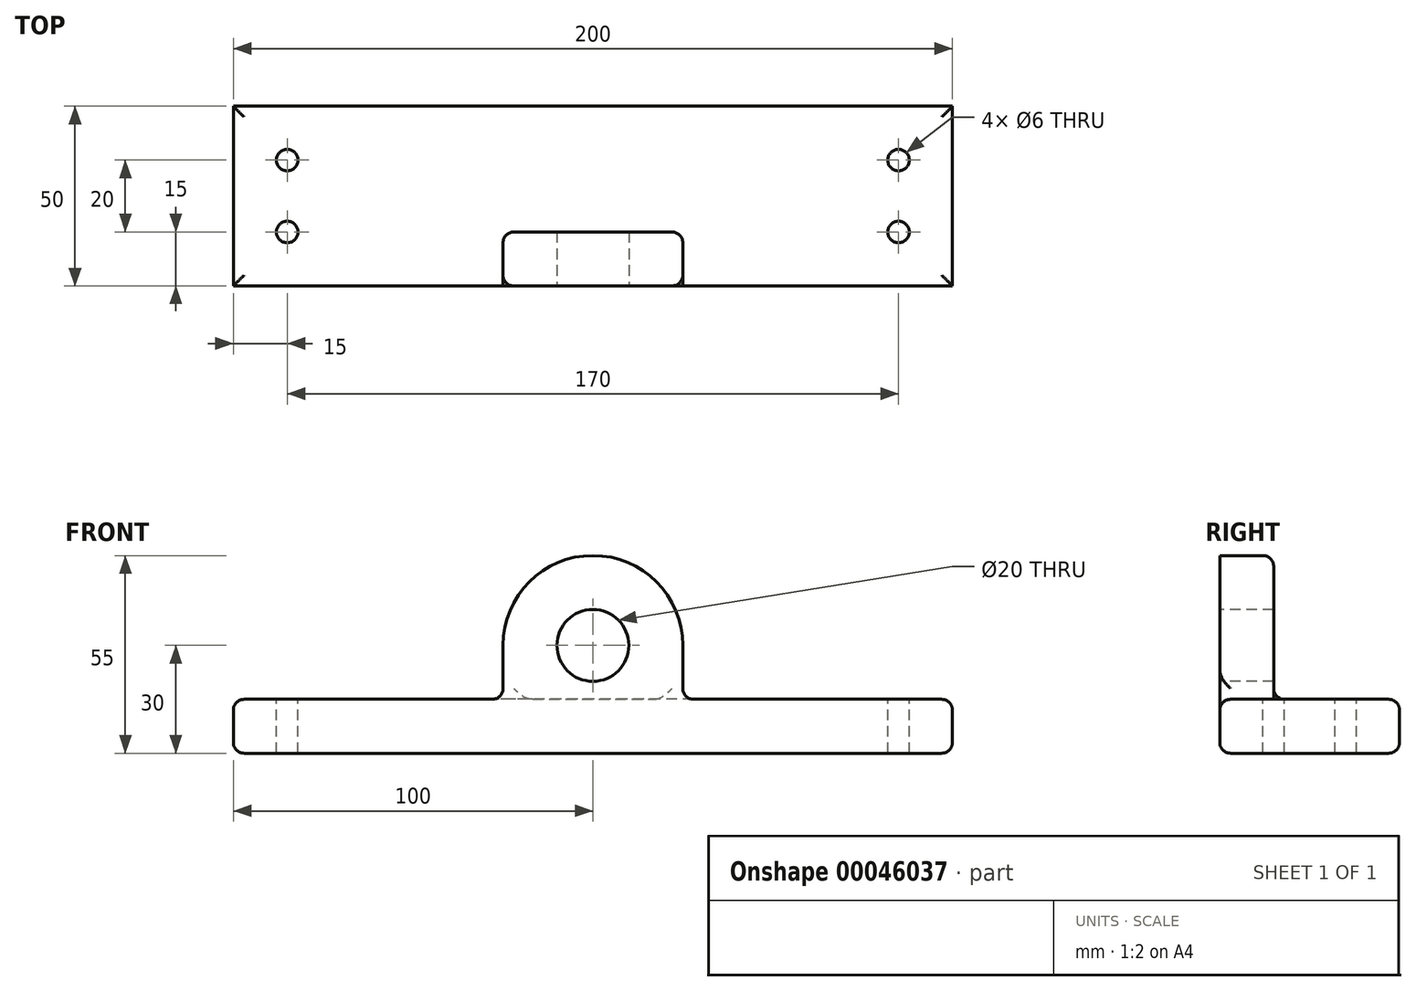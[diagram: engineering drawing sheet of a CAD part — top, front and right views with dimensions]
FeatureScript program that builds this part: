
annotation { "Feature Type Name" : "Feature", "Feature Type Description" : "" }
export const myFeature = defineFeature(function(context is Context, id is Id, definition is map)
    precondition{}
    {
        {
            var Q0;
            Q0=qCreatedBy(makeId("Top.planeOp"),FACE);
            var sketch = newSketch(context, id + "F0", { "sketchPlane" : qUnion([Q0])});
            skLineSegment(sketch, "E0.rect.bottom", {"start": v(100, -25) * mm, "end": v(-100, -25) * mm});
            skLineSegment(sketch, "E0.rect.top", {"start": v(100, 25) * mm, "end": v(-100, 25) * mm});
            skLineSegment(sketch, "E0.rect.left", {"start": v(100, -25) * mm, "end": v(100, 25) * mm});
            skLineSegment(sketch, "E0.rect.right", {"start": v(-100, -25) * mm, "end": v(-100, 25) * mm});
            skPoint(sketch, "E0.rect.middle", {"position": v(0, 0) * mm});
            skSolve(sketch);
        }
        {
            var Q0;
            Q0=makeQuery(id+"F0.imprint","IMPRINT",FACE,{"disambiguationData":[TD([[makeQuery(id+"F0.imprint","IMPRINT",EDGE,{"derivedFrom":sQuery(id+"F0.wireOp",EDGE,"E0.rect.bottom")}),-1.0]])]});
            extrude(context, id + "F1", {"entities" : qUnion([Q0]), "depth" : 15 * mm});
        }
        {
            var Q0;
            Q0=makeQuery(id+"F1.opExtrude","SWEPT_FACE",FACE,{"disambiguationData":[OSD([sQuery(id+"F0.wireOp",EDGE,"E0.rect.bottom")])]});
            var sketch = newSketch(context, id + "F2", { "sketchPlane" : qUnion([Q0])});
            skLineSegment(sketch, "E1", {"start": v(0, 0) * mm, "end": v(0, 30) * mm, "construction": true});
            skPoint(sketch, "E1.endSnap0", {"position": v(0, 15) * mm});
            skCircle(sketch, "E2", {"center": v(0, 30) * mm, "radius": 25 * mm});
            skLineSegment(sketch, "E3.bottom", {"start": v(-25, 30) * mm, "end": v(25, 30) * mm});
            skLineSegment(sketch, "E3.top", {"start": v(-25, 0) * mm, "end": v(25, 0) * mm});
            skLineSegment(sketch, "E3.left", {"start": v(-25, 30) * mm, "end": v(-25, 0) * mm});
            skLineSegment(sketch, "E3.right", {"start": v(25, 30) * mm, "end": v(25, 0) * mm});
            skCircle(sketch, "E4", {"center": v(0, 30) * mm, "radius": 10 * mm});
            skSolve(sketch);
        }
        {
            var Q0;
            {var subQ10=sQuery(id+"F2.wireOp",EDGE,"E3.top");Q0=makeQuery(id+"F2.imprint","IMPRINT",FACE,{"disambiguationData":[TD([[makeQuery(id+"F2.imprint","IMPRINT",EDGE,{"derivedFrom":subQ10}),-1.0]])]});}
            var Q1;
            {var subQ0=makeQuery(id+"F1.opExtrude","CAP_EDGE",EDGE,{"disambiguationData":[OSD([sQuery(id+"F0.wireOp",EDGE,"E0.rect.bottom")])],"isStart":false});var subQ3=sQuery(id+"F2.wireOp",EDGE,"E3.left");var subQ4=makeQuery(id+"F2.imprint","INTERSECT",VERTEX,{"derivedFrom":[subQ0,subQ3]});Q1=makeQuery(id+"F2.imprint","IMPRINT",FACE,{"disambiguationData":[TD([[makeQuery(id+"F2.imprint","IMPRINT",EDGE,{"disambiguationData":[TD([[subQ4,1.0]])],"derivedFrom":subQ0}),-1.0]])]});}
            var Q2;
            {var subQ0=makeQuery(id+"F1.opExtrude","CAP_EDGE",EDGE,{"disambiguationData":[OSD([sQuery(id+"F0.wireOp",EDGE,"E0.rect.bottom")])],"isStart":false});var subQ3=sQuery(id+"F2.wireOp",EDGE,"E3.right");var subQ4=makeQuery(id+"F2.imprint","INTERSECT",VERTEX,{"derivedFrom":[subQ0,subQ3]});Q2=makeQuery(id+"F2.imprint","IMPRINT",FACE,{"disambiguationData":[TD([[makeQuery(id+"F2.imprint","IMPRINT",EDGE,{"disambiguationData":[TD([[subQ4,-1.0]])],"derivedFrom":subQ0}),-1.0]])]});}
            var Q3;
            {var subQ0=makeQuery(id+"F1.opExtrude","CAP_EDGE",EDGE,{"disambiguationData":[OSD([sQuery(id+"F0.wireOp",EDGE,"E0.rect.bottom")])],"isStart":false});var subQ1=sQuery(id+"F2.wireOp",EDGE,"E2");var subQ3=makeQuery(id+"F2.imprint","INTERSECT",VERTEX,{"disambiguationData":[OD(0.0)],"derivedFrom":[subQ0,subQ1]});Q3=makeQuery(id+"F2.imprint","IMPRINT",FACE,{"disambiguationData":[TD([[makeQuery(id+"F2.imprint","IMPRINT",EDGE,{"disambiguationData":[TD([[subQ3,-1.0]])],"derivedFrom":subQ1}),1.0]])]});}
            var Q4;
            {var subQ3=sQuery(id+"F2.wireOp",EDGE,"E3.bottom");var subQ7=sQuery(id+"F2.wireOp",EDGE,"E4");var subQ8=makeQuery(id+"F2.imprint","INTERSECT",VERTEX,{"disambiguationData":[OD(0.0)],"derivedFrom":[subQ3,subQ7]});Q4=makeQuery(id+"F2.imprint","IMPRINT",FACE,{"disambiguationData":[TD([[makeQuery(id+"F2.imprint","IMPRINT",EDGE,{"disambiguationData":[TD([[subQ8,-1.0]])],"derivedFrom":subQ7}),-1.0]])]});}
            var Q5;
            {var subQ0=sQuery(id+"F2.wireOp",EDGE,"E4");var subQ1=sQuery(id+"F2.wireOp",EDGE,"E3.bottom");var subQ3=makeQuery(id+"F2.imprint","INTERSECT",VERTEX,{"disambiguationData":[OD(0.0)],"derivedFrom":[subQ1,subQ0]});Q5=makeQuery(id+"F2.imprint","IMPRINT",FACE,{"disambiguationData":[TD([[makeQuery(id+"F2.imprint","IMPRINT",EDGE,{"disambiguationData":[TD([[subQ3,1.0]])],"derivedFrom":subQ0}),-1.0]])]});}
            extrude(context, id + "F3", {"entities" : qUnion([Q0, Q1, Q2, Q3, Q4, Q5]), "operationType" : NewBodyOperationType.ADD, "oppositeDirection" : true, "depth" : 15 * mm});
        }
        {
            var Q0;
            Q0=makeQuery(id+"F1.opExtrude","CAP_FACE",FACE,{"disambiguationData":[OSD([sQuery(id+"F0.wireOp",EDGE,"E0.rect.bottom"),sQuery(id+"F0.wireOp",EDGE,"E0.rect.top"),sQuery(id+"F0.wireOp",EDGE,"E0.rect.left"),sQuery(id+"F0.wireOp",EDGE,"E0.rect.right")])],"isStart":false});
            var sketch = newSketch(context, id + "F4", { "sketchPlane" : qUnion([Q0])});
            skLineSegment(sketch, "E5.rect.bottom", {"start": v(85, -10) * mm, "end": v(-85, -10) * mm, "construction": true});
            skLineSegment(sketch, "E5.rect.top", {"start": v(85, 10) * mm, "end": v(-85, 10) * mm, "construction": true});
            skLineSegment(sketch, "E5.rect.left", {"start": v(85, -10) * mm, "end": v(85, 10) * mm, "construction": true});
            skLineSegment(sketch, "E5.rect.right", {"start": v(-85, -10) * mm, "end": v(-85, 10) * mm, "construction": true});
            skPoint(sketch, "E5.rect.middle", {"position": v(0, 0) * mm});
            skCircle(sketch, "E6", {"center": v(-85, 10) * mm, "radius": 3 * mm});
            skCircle(sketch, "E7", {"center": v(-85, -10) * mm, "radius": 3 * mm});
            skCircle(sketch, "E8", {"center": v(85, 10) * mm, "radius": 3 * mm});
            skCircle(sketch, "E9", {"center": v(85, -10) * mm, "radius": 3 * mm});
            skSolve(sketch);
        }
        {
            var Q0;
            Q0=makeQuery(id+"F4.imprint","IMPRINT",FACE,{"disambiguationData":[TD([[makeQuery(id+"F4.imprint","IMPRINT",EDGE,{"derivedFrom":sQuery(id+"F4.wireOp",EDGE,"E6")}),1.0]])]});
            var Q1;
            Q1=makeQuery(id+"F4.imprint","IMPRINT",FACE,{"disambiguationData":[TD([[makeQuery(id+"F4.imprint","IMPRINT",EDGE,{"derivedFrom":sQuery(id+"F4.wireOp",EDGE,"E7")}),1.0]])]});
            var Q2;
            Q2=makeQuery(id+"F4.imprint","IMPRINT",FACE,{"disambiguationData":[TD([[makeQuery(id+"F4.imprint","IMPRINT",EDGE,{"derivedFrom":sQuery(id+"F4.wireOp",EDGE,"E8")}),1.0]])]});
            var Q3;
            Q3=makeQuery(id+"F4.imprint","IMPRINT",FACE,{"disambiguationData":[TD([[makeQuery(id+"F4.imprint","IMPRINT",EDGE,{"derivedFrom":sQuery(id+"F4.wireOp",EDGE,"E9")}),1.0]])]});
            extrude(context, id + "F5", {"entities" : qUnion([Q0, Q1, Q2, Q3]), "operationType" : NewBodyOperationType.REMOVE, "endBound" : BoundingType.THROUGH_ALL, "oppositeDirection" : true, "depth" : 25 * mm});
        }
        {
            var Q0;
            {var subQ0=sQuery(id+"F0.wireOp",EDGE,"E0.rect.bottom");var subQ2=sQuery(id+"F0.wireOp",EDGE,"E0.rect.right");Q0=makeQuery(id+"F3.boolean.opBoolean","SPLIT",EDGE,{"disambiguationData":[TD([makeQuery(id+"F1.opExtrude","SWEPT_FACE",FACE,{"disambiguationData":[OSD([subQ2])]})])],"derivedFrom":makeQuery(id+"F1.opExtrude","CAP_EDGE",EDGE,{"disambiguationData":[OSD([subQ0])],"isStart":false})});}
            var Q1;
            Q1=makeQuery(id+"F1.opExtrude","CAP_EDGE",EDGE,{"disambiguationData":[OSD([sQuery(id+"F0.wireOp",EDGE,"E0.rect.right")])],"isStart":false});
            var Q2;
            Q2=makeQuery(id+"F1.opExtrude","CAP_EDGE",EDGE,{"disambiguationData":[OSD([sQuery(id+"F0.wireOp",EDGE,"E0.rect.top")])],"isStart":false});
            var Q3;
            Q3=makeQuery(id+"F1.opExtrude","CAP_EDGE",EDGE,{"disambiguationData":[OSD([sQuery(id+"F0.wireOp",EDGE,"E0.rect.left")])],"isStart":false});
            var Q4;
            {var subQ0=sQuery(id+"F0.wireOp",EDGE,"E0.rect.bottom");var subQ2=sQuery(id+"F0.wireOp",EDGE,"E0.rect.left");Q4=makeQuery(id+"F3.boolean.opBoolean","SPLIT",EDGE,{"disambiguationData":[TD([makeQuery(id+"F1.opExtrude","SWEPT_FACE",FACE,{"disambiguationData":[OSD([subQ2])]})])],"derivedFrom":makeQuery(id+"F1.opExtrude","CAP_EDGE",EDGE,{"disambiguationData":[OSD([subQ0])],"isStart":false})});}
            var Q5;
            Q5=makeQuery(id+"F3.boolean.opBoolean","INTERSECT",EDGE,{"derivedFrom":[makeQuery(id+"F1.opExtrude","CAP_FACE",FACE,{"disambiguationData":[OSD([sQuery(id+"F0.wireOp",EDGE,"E0.rect.bottom"),sQuery(id+"F0.wireOp",EDGE,"E0.rect.top"),sQuery(id+"F0.wireOp",EDGE,"E0.rect.left"),sQuery(id+"F0.wireOp",EDGE,"E0.rect.right")])],"isStart":false}),makeQuery(id+"F3.opExtrude","SWEPT_FACE",FACE,{"disambiguationData":[OSD([sQuery(id+"F2.wireOp",EDGE,"E3.right")])]})]});
            var Q6;
            Q6=makeQuery(id+"F3.boolean.opBoolean","INTERSECT",EDGE,{"derivedFrom":[makeQuery(id+"F1.opExtrude","CAP_FACE",FACE,{"disambiguationData":[OSD([sQuery(id+"F0.wireOp",EDGE,"E0.rect.bottom"),sQuery(id+"F0.wireOp",EDGE,"E0.rect.top"),sQuery(id+"F0.wireOp",EDGE,"E0.rect.left"),sQuery(id+"F0.wireOp",EDGE,"E0.rect.right")])],"isStart":false}),makeQuery(id+"F3.opExtrude","SWEPT_FACE",FACE,{"disambiguationData":[OSD([sQuery(id+"F2.wireOp",EDGE,"E3.left")])]})]});
            var Q7;
            Q7=makeQuery(id+"F3.opExtrude","CAP_EDGE",EDGE,{"disambiguationData":[OSD([sQuery(id+"F2.wireOp",EDGE,"E3.left")])],"isStart":false});
            var Q8;
            Q8=makeQuery(id+"F1.opExtrude","CAP_EDGE",EDGE,{"disambiguationData":[OSD([sQuery(id+"F0.wireOp",EDGE,"E0.rect.bottom")])],"isStart":true});
            var Q9;
            Q9=makeQuery(id+"F1.opExtrude","CAP_EDGE",EDGE,{"disambiguationData":[OSD([sQuery(id+"F0.wireOp",EDGE,"E0.rect.left")])],"isStart":true});
            var Q10;
            Q10=makeQuery(id+"F1.opExtrude","CAP_EDGE",EDGE,{"disambiguationData":[OSD([sQuery(id+"F0.wireOp",EDGE,"E0.rect.top")])],"isStart":true});
            var Q11;
            Q11=makeQuery(id+"F1.opExtrude","CAP_EDGE",EDGE,{"disambiguationData":[OSD([sQuery(id+"F0.wireOp",EDGE,"E0.rect.right")])],"isStart":true});
            fillet(context, id + "F6", {"entities" : qUnion([Q0, Q1, Q2, Q3, Q4, Q5, Q6, Q7, Q8, Q9, Q10, Q11]), "radius" : 3 * mm, "tangentPropagation" : true, "allowEdgeOverflow" : false});
        }
    });
